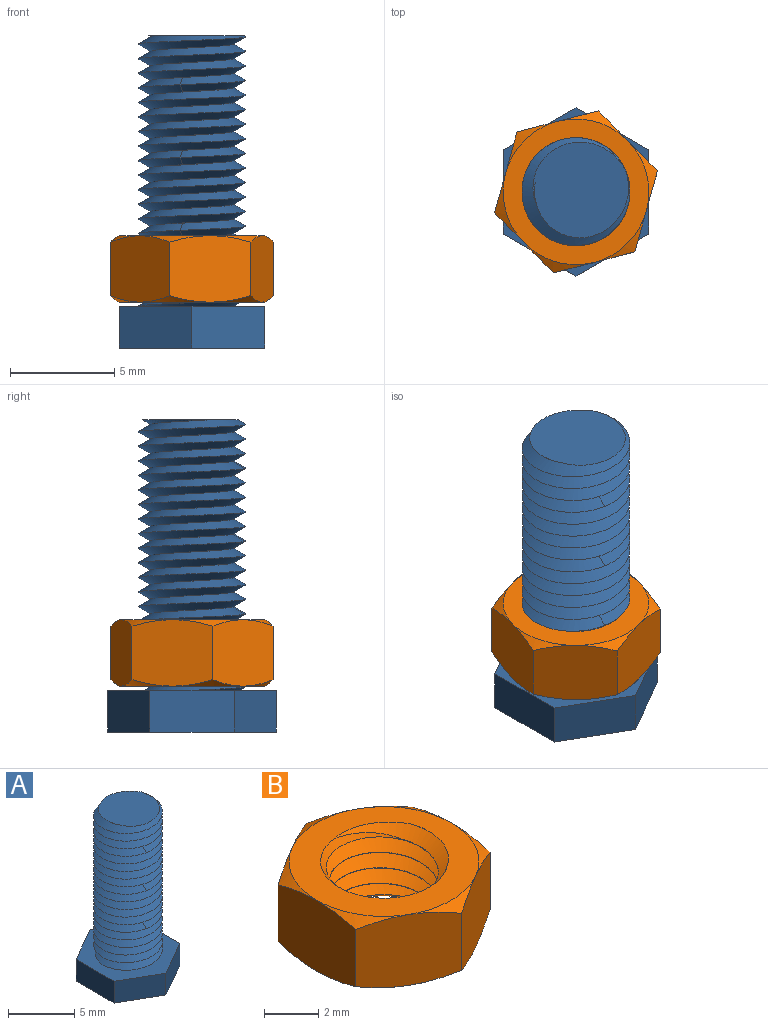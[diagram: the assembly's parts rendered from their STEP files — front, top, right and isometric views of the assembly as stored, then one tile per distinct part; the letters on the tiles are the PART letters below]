
ASSEMBLY  parts=2 mates=1
PART A: 18 faces, bbox 7.5x8.6x15.9 mm
  f0: cylinder r=2mm len=13mm, axis (0,0,-1), area 4.2mm2, adj f1,f2,f3,f4,f5,f6,f7,f8
  f1: plane 5.09x5.09mm, normal (0,0,1), area 16.6mm2, adj f0,f2,f3
  f2: bspline ~5.99x5.19mm, area 35.5mm2, adj f0,f1,f3,f8
  f3: bspline ~5.99x5.19mm, area 30.8mm2, adj f0,f1,f2,f9
  f4: bspline ~5.99x5.19mm, area 54mm2, adj f0,f5,f7,f10
  f5: bspline ~5.99x5.19mm, area 49.4mm2, adj f0,f4,f6,f10
  f6: bspline ~5.99x5.19mm, area 49.5mm2, adj f0,f5,f7,f8
  f7: bspline ~5.99x5.19mm, area 49.5mm2, adj f0,f4,f6,f9
  f8: bspline ~5.99x5.19mm, area 49.5mm2, adj f0,f2,f6,f9
  f9: bspline ~5.99x5.19mm, area 49.5mm2, adj f0,f3,f7,f8
  f10: plane 8.55x7.47mm, normal (0,0,1), area 25.9mm2, adj f0,f4,f5,f11,f12,f13,f14,f15
  f11: plane 4.04x2mm, normal (1,0,0), area 8.1mm2, adj f10,f12,f16,f17
  f12: plane 3.5x2.02mm, normal (0.5,0.87,0), area 8.1mm2, adj f10,f11,f13,f17
  f13: plane 3.5x2.02mm, normal (-0.5,0.87,0), area 8.1mm2, adj f10,f12,f14,f17
  f14: plane 4.04x2mm, normal (-1,0,0), area 8.1mm2, adj f10,f13,f15,f17
  f15: plane 3.5x2.02mm, normal (-0.5,-0.87,0), area 8.1mm2, adj f10,f14,f16,f17
  f16: plane 3.5x2.02mm, normal (0.5,-0.87,0), area 8.1mm2, adj f10,f11,f15,f17
  f17: plane 8.08x7mm, normal (0,0,-1), area 42.4mm2, adj f11,f12,f13,f14,f15,f16
PART B: 25 faces, bbox 8.4x8.4x4.4 mm
  f0: plane 3.83x3.54mm, normal (0.5,-0.87,0), area 12.1mm2, adj f1,f5,f13,f14,f15,f16
  f1: plane 4.38x3.54mm, normal (1,0,0), area 12.1mm2, adj f0,f2,f9,f14,f15,f20
  f2: plane 3.83x3.54mm, normal (0.5,0.87,0), area 12.1mm2, adj f1,f3,f9,f10,f19,f20
  f3: plane 3.83x3.54mm, normal (-0.5,0.87,0), area 12.1mm2, adj f2,f4,f10,f11,f18,f19
  f4: plane 4.38x3.54mm, normal (-1,0,0), area 12.1mm2, adj f3,f5,f11,f12,f17,f18
  f5: plane 3.83x3.54mm, normal (-0.5,-0.87,0), area 12.1mm2, adj f0,f4,f12,f13,f16,f17
  f6: plane 7.12x7.12mm, normal (0,0,-1), area 20.5mm2, adj f15,f16,f17,f18,f19,f20,f22,f23
  f7: plane 7.1x7.1mm, normal (0,0,1), area 20.5mm2, adj f9,f10,f11,f12,f13,f14,f21,f23
  f8: cylinder r=2mm len=4mm, axis (0,0,-1), area 1mm2, adj f21,f22,f23,f24
  f9: cone r=3.5mm half-angle=60deg, axis (0,0,-1), area 1.2mm2, adj f1,f2,f7
  f10: cone r=3.5mm half-angle=60deg, axis (0,0,-1), area 1.2mm2, adj f2,f3,f7
  f11: cone r=3.5mm half-angle=60deg, axis (0,0,-1), area 1.2mm2, adj f3,f4,f7
  f12: cone r=3.5mm half-angle=60deg, axis (0,0,-1), area 1.2mm2, adj f4,f5,f7
  f13: cone r=3.5mm half-angle=60deg, axis (0,0,-1), area 1.2mm2, adj f0,f5,f7
  f14: cone r=3.5mm half-angle=60deg, axis (0,0,-1), area 1.2mm2, adj f0,f1,f7
  f15: cone r=3.5mm half-angle=60deg, axis (0,0,1), area 1.2mm2, adj f0,f1,f6
  f16: cone r=3.5mm half-angle=60deg, axis (0,0,1), area 1.2mm2, adj f0,f5,f6
  f17: cone r=3.5mm half-angle=60deg, axis (0,0,1), area 1.2mm2, adj f4,f5,f6
  f18: cone r=3.5mm half-angle=60deg, axis (0,0,1), area 1.2mm2, adj f3,f4,f6
  f19: cone r=3.5mm half-angle=60deg, axis (0,0,1), area 1.2mm2, adj f2,f3,f6
  f20: cone r=3.5mm half-angle=60deg, axis (0,0,1), area 1.2mm2, adj f1,f2,f6
  f21: cone r=2mm half-angle=45deg, axis (0,0,1), area 2mm2, adj f7,f8,f23,f24
  f22: cone r=2.34mm half-angle=45deg, axis (0,0,-1), area 2mm2, adj f6,f8,f23,f24
  f23: bspline ~5.99x5.19mm, area 42.8mm2, adj f6,f7,f8,f21,f22,f24
  f24: bspline ~5.99x5.19mm, area 42.8mm2, adj f6,f7,f8,f21,f22,f23
PLACE A at identity fixed
PLACE B rot(axis=(0,0,1),104.5deg) t=(0,0,0.2)mm
MATE cylindrical A.f0 <-> B.f8  axis (0,0,1) through (0,0,0)mm
